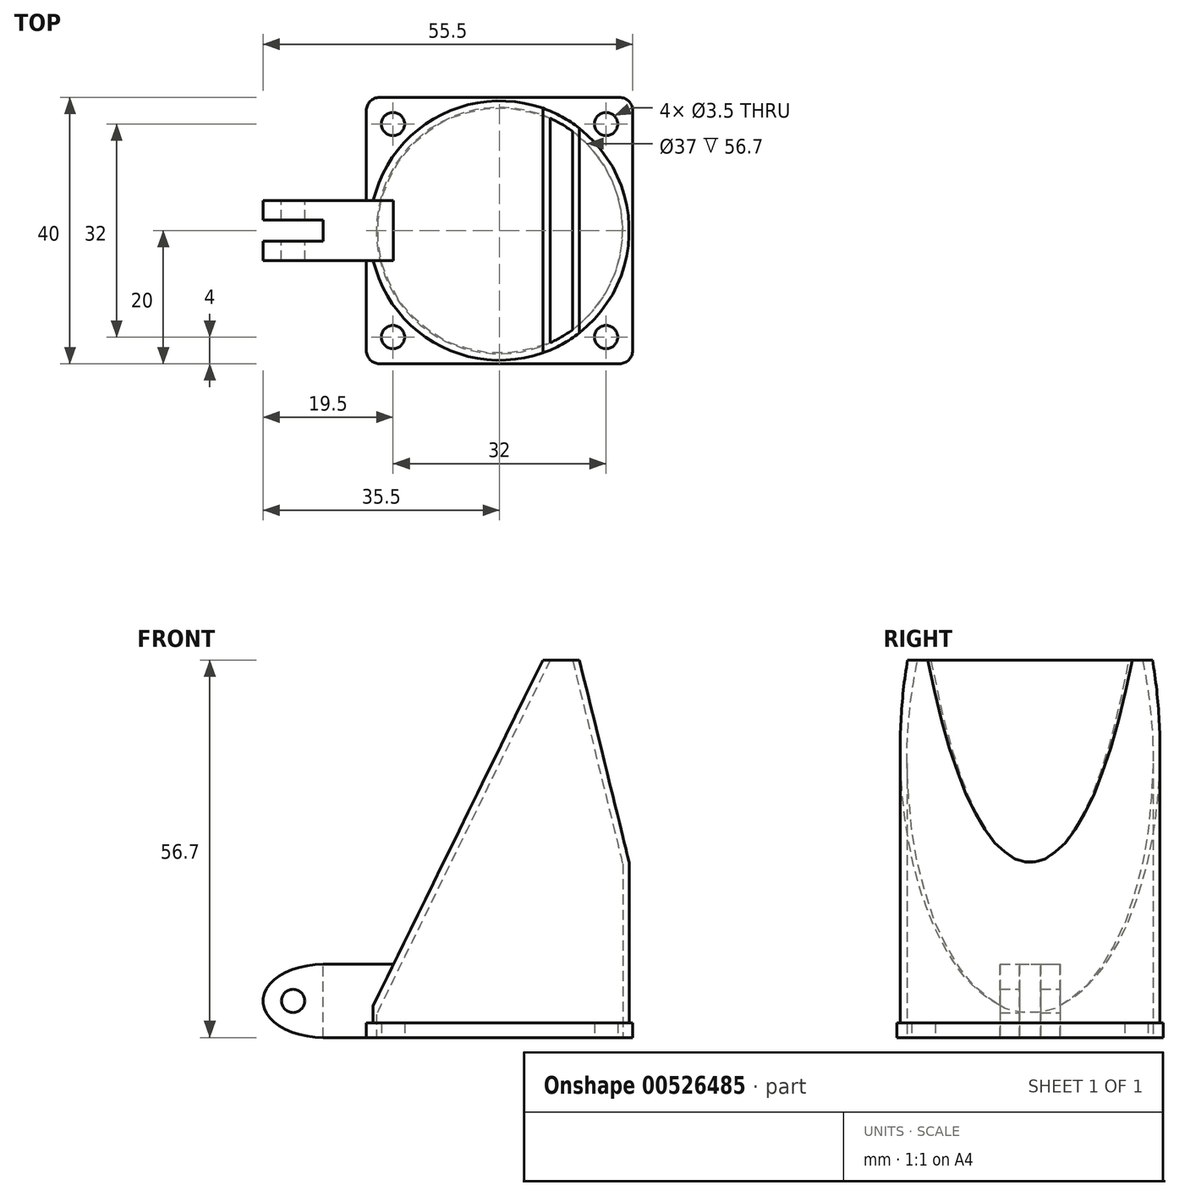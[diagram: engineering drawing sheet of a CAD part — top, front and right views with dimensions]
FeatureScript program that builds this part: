
annotation { "Feature Type Name" : "Feature", "Feature Type Description" : "" }
export const myFeature = defineFeature(function(context is Context, id is Id, definition is map)
    precondition{}
    {
        {
            var Q0;
            Q0=qCreatedBy(makeId("Top.planeOp"),FACE);
            var sketch = newSketch(context, id + "F0", { "sketchPlane" : qUnion([Q0])});
            skLineSegment(sketch, "E0.bottom", {"start": v(20, -20) * mm, "end": v(-20, -20) * mm});
            skLineSegment(sketch, "E0.top", {"start": v(20, 20) * mm, "end": v(-20, 20) * mm});
            skLineSegment(sketch, "E0.left", {"start": v(20, -20) * mm, "end": v(20, 20) * mm});
            skLineSegment(sketch, "E0.right", {"start": v(-20, -20) * mm, "end": v(-20, 20) * mm});
            skPoint(sketch, "E0.middle", {"position": v(0, 0) * mm});
            skCircle(sketch, "E1", {"center": v(16, -16) * mm, "radius": 1.75 * mm});
            skCircle(sketch, "E2", {"center": v(-16, -16) * mm, "radius": 1.75 * mm});
            skCircle(sketch, "E3", {"center": v(-16, 16) * mm, "radius": 1.75 * mm});
            skCircle(sketch, "E4", {"center": v(16, 16) * mm, "radius": 1.75 * mm});
            skLineSegment(sketch, "E5", {"start": v(0, -20) * mm, "end": v(0, 20) * mm, "construction": true});
            skLineSegment(sketch, "E6", {"start": v(0, 0) * mm, "end": v(20, 0) * mm, "construction": true});
            skCircle(sketch, "E7", {"center": v(0, 0) * mm, "radius": 18.5 * mm});
            skSolve(sketch);
        }
        {
            var Q0;
            Q0 = qSketchRegion(id + "F0", true);
            extrude(context, id + "F1", {"entities" : qUnion([Q0]), "depth" : 2.2 * mm, "offsetDistance" : 25 * mm});
        }
        {
            var Q0;
            Q0=makeQuery(id+"F1.opExtrude","CAP_FACE",FACE,{"disambiguationData":[OSD([sQuery(id+"F0.wireOp",EDGE,"E0.bottom"),sQuery(id+"F0.wireOp",EDGE,"E0.top"),sQuery(id+"F0.wireOp",EDGE,"E0.left"),sQuery(id+"F0.wireOp",EDGE,"E0.right"),sQuery(id+"F0.wireOp",EDGE,"E1"),sQuery(id+"F0.wireOp",EDGE,"E2"),sQuery(id+"F0.wireOp",EDGE,"E3"),sQuery(id+"F0.wireOp",EDGE,"E4")])],"isStart":false});
            var sketch = newSketch(context, id + "F2", { "sketchPlane" : qUnion([Q0])});
            skCircle(sketch, "E8.0", {"center": v(0, 0) * mm, "radius": 19.5 * mm});
            skSolve(sketch);
        }
        {
            var Q0;
            Q0 = qSketchRegion(id + "F2", true);
            extrude(context, id + "F3", {"entities" : qUnion([Q0]), "depth" : 54.5 * mm, "offsetDistance" : 25 * mm});
        }
        {
            var Q0;
            Q0=qCreatedBy(makeId("Front.planeOp"),FACE);
            var sketch = newSketch(context, id + "F4", { "sketchPlane" : qUnion([Q0])});
            skLineSegment(sketch, "E9", {"start": v(19.5, 26.2) * mm, "end": v(12, 56.7) * mm});
            skLineSegment(sketch, "E10", {"start": v(12, 56.7) * mm, "end": v(6.5, 56.7) * mm});
            skLineSegment(sketch, "E11", {"start": v(6.5, 56.7) * mm, "end": v(-19.5, 3.7) * mm});
            skLineSegment(sketch, "E12", {"start": v(-19.5, 3.7) * mm, "end": v(-19.5, 57.7) * mm});
            skLineSegment(sketch, "E13", {"start": v(-19.5, 57.7) * mm, "end": v(19.5, 57.7) * mm});
            skLineSegment(sketch, "E14", {"start": v(19.5, 57.7) * mm, "end": v(19.5, 26.2) * mm});
            skLineSegment(sketch, "E15", {"start": v(19.5, 56.7) * mm, "end": v(19.5, 2.2) * mm});
            skLineSegment(sketch, "E16", {"start": v(19.5, 56.7) * mm, "end": v(19.5, 2.2) * mm, "construction": true});
            skLineSegment(sketch, "E17", {"start": v(-19.5, 7.82) * mm, "end": v(-19.5, 56.7) * mm, "construction": true});
            skSolve(sketch);
        }
        {
            var Q0;
            Q0 = qSketchRegion(id + "F4", true);
            extrude(context, id + "F5", {"entities" : qUnion([Q0]), "operationType" : NewBodyOperationType.REMOVE, "endBound" : BoundingType.THROUGH_ALL, "oppositeDirection" : true, "depth" : 25 * mm, "offsetDistance" : 25 * mm, "hasSecondDirection" : true, "secondDirectionBound" : BoundingType.THROUGH_ALL, "secondDirectionOppositeDirection" : false, "secondDirectionDepth" : 25 * mm});
        }
        {
            var Q0;
            Q0=makeQuery(id+"F3.opExtrude","CAP_FACE",FACE,{"disambiguationData":[OSD([sQuery(id+"F2.wireOp",EDGE,"E8.0")])],"isStart":true});
            var Q1;
            Q1=makeQuery(id+"F3.opExtrude","CAP_FACE",FACE,{"disambiguationData":[OSD([sQuery(id+"F2.wireOp",EDGE,"E8.0")])],"isStart":false});
            shell(context, id + "F6", {"entities" : qUnion([Q0, Q1]), "thickness" : 1 * mm});
        }
        {
            var Q0;
            Q0=makeQuery(id+"F3.opExtrude","SWEPT_BODY",BODY,{"disambiguationData":[OSD([sQuery(id+"F2.wireOp",EDGE,"E8.0")])]});
            var Q1;
            Q1=makeQuery(id+"F1.opExtrude","SWEPT_BODY",BODY,{"disambiguationData":[OSD([sQuery(id+"F0.wireOp",EDGE,"E0.bottom"),sQuery(id+"F0.wireOp",EDGE,"E0.top"),sQuery(id+"F0.wireOp",EDGE,"E0.left"),sQuery(id+"F0.wireOp",EDGE,"E0.right"),sQuery(id+"F0.wireOp",EDGE,"E1"),sQuery(id+"F0.wireOp",EDGE,"E2"),sQuery(id+"F0.wireOp",EDGE,"E3"),sQuery(id+"F0.wireOp",EDGE,"E4"),sQuery(id+"F0.wireOp",EDGE,"E7")])]});
            booleanBodies(context, id + "F7", {"operationType" : BooleanOperationType.UNION, "tools" : qUnion([Q0, Q1])});
        }
        {
            var Q0;
            Q0=qCreatedBy(makeId("Front.planeOp"),FACE);
            var sketch = newSketch(context, id + "F8", { "sketchPlane" : qUnion([Q0])});
            skEllipticalArc(sketch, "E18", {});
            skLineSegment(sketch, "E19", {"start": v(-20, 0) * mm, "end": v(-26.5, 0) * mm});
            skLineSegment(sketch, "E20", {"start": v(-18.5, 5.74) * mm, "end": v(-15.92, 11) * mm});
            skLineSegment(sketch, "E21", {"start": v(-15.92, 11) * mm, "end": v(-26.5, 11) * mm});
            skCircle(sketch, "E22", {"center": v(-31, 5.5) * mm, "radius": 1.75 * mm});
            skLineSegment(sketch, "E23", {"start": v(18.5, 26.08) * mm, "end": v(18.5, 0) * mm});
            skLineSegment(sketch, "E24", {"start": v(-18.5, 0) * mm, "end": v(-18.5, 3.47) * mm});
            skLineSegment(sketch, "E25", {"start": v(-20, 0) * mm, "end": v(-18.5, 0) * mm});
            skLineSegment(sketch, "E26", {"start": v(-18.5, 3.47) * mm, "end": v(-18.5, 5.74) * mm});
            const initialGuessF8  = {"E18": [-0.0265, 0.0055, -1, 0, 0.009, 0.0055, 4.71238898038469, 1.5707963267948966]};
            skSetInitialGuess(sketch, initialGuessF8);
            skSolve(sketch);
        }
        {
            var Q0;
            Q0 = qSketchRegion(id + "F8", true);
            extrude(context, id + "F9", {"entities" : qUnion([Q0]), "operationType" : NewBodyOperationType.ADD, "depth" : 4.5 * mm, "offsetDistance" : 25 * mm, "hasSecondDirection" : true, "secondDirectionOppositeDirection" : true, "secondDirectionDepth" : 4.5 * mm});
        }
        {
            var Q0;
            Q0=makeQuery(id+"F9.opExtrude","SWEPT_FACE",FACE,{"disambiguationData":[OSD([sQuery(id+"F8.wireOp",EDGE,"E21")])]});
            var sketch = newSketch(context, id + "F10", { "sketchPlane" : qUnion([Q0])});
            skLineSegment(sketch, "E27.bottom", {"start": v(-26.5, -1.6) * mm, "end": v(-35.5, -1.6) * mm});
            skLineSegment(sketch, "E27.top", {"start": v(-26.5, 1.6) * mm, "end": v(-35.5, 1.6) * mm});
            skLineSegment(sketch, "E27.left", {"start": v(-26.5, -1.6) * mm, "end": v(-26.5, 1.6) * mm});
            skLineSegment(sketch, "E27.right", {"start": v(-35.5, -1.6) * mm, "end": v(-35.5, 1.6) * mm});
            skLineSegment(sketch, "E28", {"start": v(-15.92, 0) * mm, "end": v(-42.65, 0) * mm, "construction": true});
            skSolve(sketch);
        }
        {
            var Q0;
            Q0 = qSketchRegion(id + "F10", true);
            extrude(context, id + "F11", {"entities" : qUnion([Q0]), "operationType" : NewBodyOperationType.REMOVE, "endBound" : BoundingType.THROUGH_ALL, "oppositeDirection" : true, "depth" : 25 * mm, "offsetDistance" : 25 * mm});
        }
        {
            var Q0;
            Q0=makeQuery(id+"F1.opExtrude","SWEPT_EDGE",EDGE,{"disambiguationData":[OSD([sQuery(id+"F0.wireOp",EDGE,"E0.top"),sQuery(id+"F0.wireOp",EDGE,"E0.left")])]});
            var Q1;
            Q1=makeQuery(id+"F1.opExtrude","SWEPT_EDGE",EDGE,{"disambiguationData":[OSD([sQuery(id+"F0.wireOp",EDGE,"E0.top"),sQuery(id+"F0.wireOp",EDGE,"E0.right")])]});
            var Q2;
            Q2=makeQuery(id+"F1.opExtrude","SWEPT_EDGE",EDGE,{"disambiguationData":[OSD([sQuery(id+"F0.wireOp",EDGE,"E0.bottom"),sQuery(id+"F0.wireOp",EDGE,"E0.right")])]});
            var Q3;
            Q3=makeQuery(id+"F1.opExtrude","SWEPT_EDGE",EDGE,{"disambiguationData":[OSD([sQuery(id+"F0.wireOp",EDGE,"E0.bottom"),sQuery(id+"F0.wireOp",EDGE,"E0.left")])]});
            fillet(context, id + "F12", {"entities" : qUnion([Q0, Q1, Q2, Q3]), "radius" : 2 * mm, "tangentPropagation" : true, "allowEdgeOverflow" : false});
        }
    });
